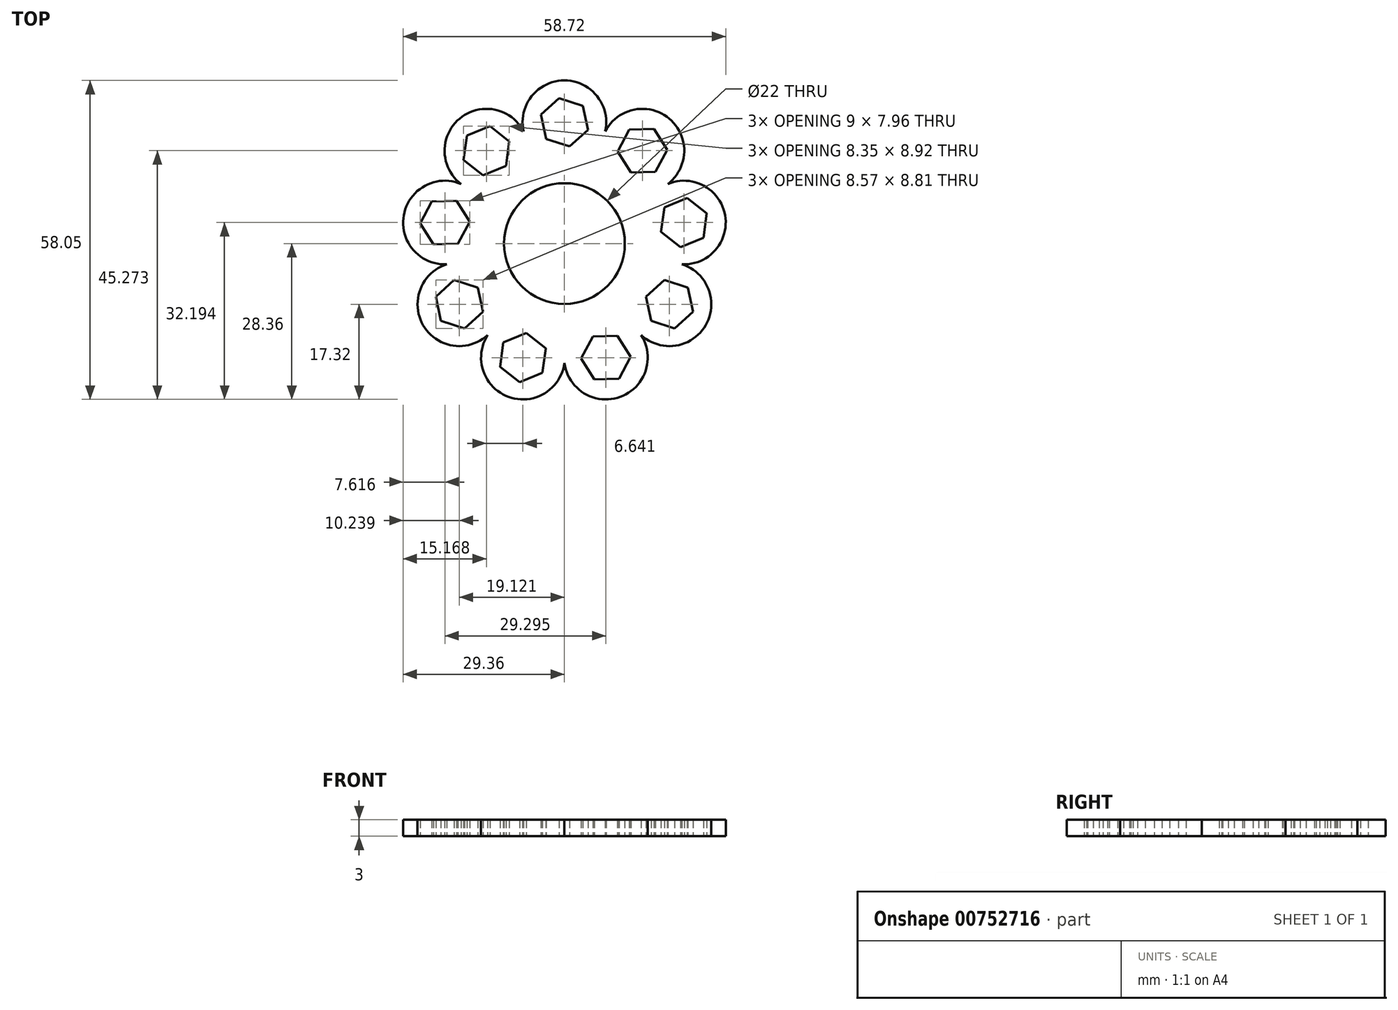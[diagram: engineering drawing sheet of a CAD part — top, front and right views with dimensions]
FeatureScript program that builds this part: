
annotation { "Feature Type Name" : "Feature", "Feature Type Description" : "" }
export const myFeature = defineFeature(function(context is Context, id is Id, definition is map)
    precondition{}
    {
        {
            var Q0;
            Q0=qCreatedBy(makeId("Top.planeOp"),FACE);
            var sketch = newSketch(context, id + "F0", { "sketchPlane" : qUnion([Q0])});
            skLineSegment(sketch, "E0.0", {"start": v(4.28, 20.7) * mm, "end": v(0.94, 17.68) * mm});
            skLineSegment(sketch, "E0.1", {"start": v(0.94, 17.68) * mm, "end": v(-3.34, 19.06) * mm});
            skLineSegment(sketch, "E0.2", {"start": v(-3.34, 19.06) * mm, "end": v(-4.28, 23.47) * mm});
            skLineSegment(sketch, "E0.3", {"start": v(-4.28, 23.47) * mm, "end": v(-0.94, 26.48) * mm});
            skLineSegment(sketch, "E0.4", {"start": v(-0.94, 26.48) * mm, "end": v(3.34, 25.1) * mm});
            skLineSegment(sketch, "E0.5", {"start": v(3.34, 25.1) * mm, "end": v(4.28, 20.7) * mm});
            skPoint(sketch, "E1.1.0", {"position": v(-10.33, 16.38) * mm});
            skLineSegment(sketch, "E1.1.1", {"start": v(-13.57, 21.37) * mm, "end": v(-10.02, 18.6) * mm});
            skLineSegment(sketch, "E1.1.5", {"start": v(-14.81, 12.45) * mm, "end": v(-18.37, 15.22) * mm});
            skLineSegment(sketch, "E1.1.6", {"start": v(-10.64, 14.15) * mm, "end": v(-14.81, 12.45) * mm});
            skLineSegment(sketch, "E1.1.7", {"start": v(-18.37, 15.22) * mm, "end": v(-17.74, 19.68) * mm});
            skLineSegment(sketch, "E1.1.9", {"start": v(-10.02, 18.6) * mm, "end": v(-10.64, 14.15) * mm});
            skLineSegment(sketch, "E1.1.10", {"start": v(-17.74, 19.68) * mm, "end": v(-13.57, 21.37) * mm});
            skPoint(sketch, "E1.2.0", {"position": v(-18.44, 5.9) * mm});
            skLineSegment(sketch, "E1.2.1", {"start": v(-24.13, 7.65) * mm, "end": v(-19.63, 7.81) * mm});
            skLineSegment(sketch, "E1.2.5", {"start": v(-19.35, 0.02) * mm, "end": v(-23.85, -0.14) * mm});
            skLineSegment(sketch, "E1.2.6", {"start": v(-17.24, 4) * mm, "end": v(-19.35, 0.02) * mm});
            skLineSegment(sketch, "E1.2.7", {"start": v(-23.85, -0.14) * mm, "end": v(-26.24, 3.67) * mm});
            skLineSegment(sketch, "E1.2.9", {"start": v(-19.63, 7.81) * mm, "end": v(-17.24, 4) * mm});
            skLineSegment(sketch, "E1.2.10", {"start": v(-26.24, 3.67) * mm, "end": v(-24.13, 7.65) * mm});
            skPoint(sketch, "E1.3.0", {"position": v(-17.92, -7.33) * mm});
            skLineSegment(sketch, "E1.3.1", {"start": v(-23.4, -9.65) * mm, "end": v(-20.06, -6.64) * mm});
            skLineSegment(sketch, "E1.3.5", {"start": v(-14.84, -12.43) * mm, "end": v(-18.18, -15.44) * mm});
            skLineSegment(sketch, "E1.3.6", {"start": v(-15.78, -8.02) * mm, "end": v(-14.84, -12.43) * mm});
            skLineSegment(sketch, "E1.3.7", {"start": v(-18.18, -15.44) * mm, "end": v(-22.46, -14.06) * mm});
            skLineSegment(sketch, "E1.3.9", {"start": v(-20.06, -6.64) * mm, "end": v(-15.78, -8.02) * mm});
            skLineSegment(sketch, "E1.3.10", {"start": v(-22.46, -14.06) * mm, "end": v(-23.4, -9.65) * mm});
            skPoint(sketch, "E1.4.0", {"position": v(-9.02, -17.13) * mm});
            skLineSegment(sketch, "E1.4.1", {"start": v(-11.72, -22.44) * mm, "end": v(-11.1, -17.98) * mm});
            skLineSegment(sketch, "E1.4.5", {"start": v(-3.38, -19.06) * mm, "end": v(-4, -23.52) * mm});
            skLineSegment(sketch, "E1.4.6", {"start": v(-6.93, -16.29) * mm, "end": v(-3.38, -19.06) * mm});
            skLineSegment(sketch, "E1.4.7", {"start": v(-4, -23.52) * mm, "end": v(-8.17, -25.2) * mm});
            skLineSegment(sketch, "E1.4.9", {"start": v(-11.1, -17.98) * mm, "end": v(-6.93, -16.29) * mm});
            skLineSegment(sketch, "E1.4.10", {"start": v(-8.17, -25.2) * mm, "end": v(-11.72, -22.44) * mm});
            skPoint(sketch, "E1.5.0", {"position": v(4.1, -18.92) * mm});
            skLineSegment(sketch, "E1.5.1", {"start": v(5.44, -24.73) * mm, "end": v(3.05, -20.9) * mm});
            skLineSegment(sketch, "E1.5.5", {"start": v(9.66, -16.77) * mm, "end": v(12.05, -20.58) * mm});
            skLineSegment(sketch, "E1.5.6", {"start": v(5.16, -16.93) * mm, "end": v(9.66, -16.77) * mm});
            skLineSegment(sketch, "E1.5.7", {"start": v(12.05, -20.58) * mm, "end": v(9.94, -24.56) * mm});
            skLineSegment(sketch, "E1.5.9", {"start": v(3.05, -20.9) * mm, "end": v(5.16, -16.93) * mm});
            skLineSegment(sketch, "E1.5.10", {"start": v(9.94, -24.56) * mm, "end": v(5.44, -24.73) * mm});
            skPoint(sketch, "E1.6.0", {"position": v(15.3, -11.85) * mm});
            skLineSegment(sketch, "E1.6.1", {"start": v(20.06, -15.44) * mm, "end": v(15.78, -14.06) * mm});
            skLineSegment(sketch, "E1.6.5", {"start": v(18.18, -6.64) * mm, "end": v(22.46, -8.02) * mm});
            skLineSegment(sketch, "E1.6.6", {"start": v(14.84, -9.65) * mm, "end": v(18.18, -6.64) * mm});
            skLineSegment(sketch, "E1.6.7", {"start": v(22.46, -8.02) * mm, "end": v(23.4, -12.43) * mm});
            skLineSegment(sketch, "E1.6.9", {"start": v(15.78, -14.06) * mm, "end": v(14.84, -9.65) * mm});
            skLineSegment(sketch, "E1.6.10", {"start": v(23.4, -12.43) * mm, "end": v(20.06, -15.44) * mm});
            skLineSegment(sketch, "E1.7.1", {"start": v(25.3, 1.07) * mm, "end": v(21.12, -0.63) * mm});
            skLineSegment(sketch, "E1.7.5", {"start": v(18.2, 6.6) * mm, "end": v(22.36, 8.3) * mm});
            skLineSegment(sketch, "E1.7.6", {"start": v(17.57, 2.14) * mm, "end": v(18.2, 6.6) * mm});
            skLineSegment(sketch, "E1.7.7", {"start": v(22.36, 8.3) * mm, "end": v(25.92, 5.53) * mm});
            skLineSegment(sketch, "E1.7.9", {"start": v(21.12, -0.63) * mm, "end": v(17.57, 2.14) * mm});
            skLineSegment(sketch, "E1.7.10", {"start": v(25.92, 5.53) * mm, "end": v(25.3, 1.07) * mm});
            skPoint(sketch, "E1.8.0", {"position": v(14.33, 13.02) * mm});
            skLineSegment(sketch, "E1.8.1", {"start": v(18.7, 17.08) * mm, "end": v(16.58, 13.1) * mm});
            skLineSegment(sketch, "E1.8.5", {"start": v(9.7, 16.75) * mm, "end": v(11.8, 20.73) * mm});
            skLineSegment(sketch, "E1.8.6", {"start": v(12.08, 12.93) * mm, "end": v(9.7, 16.75) * mm});
            skLineSegment(sketch, "E1.8.7", {"start": v(11.8, 20.73) * mm, "end": v(16.3, 20.9) * mm});
            skLineSegment(sketch, "E1.8.9", {"start": v(16.58, 13.1) * mm, "end": v(12.08, 12.93) * mm});
            skLineSegment(sketch, "E1.8.10", {"start": v(16.3, 20.9) * mm, "end": v(18.7, 17.08) * mm});
            skArc(sketch, "E2.trimOffspring", {"start": v(7.43, 20.41) * mm, "mid": v(0, 29.7) * mm, "end": v(-7.43, 20.41) * mm});
            skArc(sketch, "E3.trimOffspring", {"start": v(18.81, 10.86) * mm, "mid": v(19.09, 22.75) * mm, "end": v(7.43, 20.41) * mm});
            skArc(sketch, "E4.trimOffspring", {"start": v(21.4, -3.77) * mm, "mid": v(29.24, 5.16) * mm, "end": v(18.81, 10.86) * mm});
            skArc(sketch, "E5.trimOffspring", {"start": v(13.96, -16.64) * mm, "mid": v(25.72, -14.85) * mm, "end": v(21.4, -3.77) * mm});
            skArc(sketch, "E6.trimOffspring", {"start": v(0, -21.72) * mm, "mid": v(10.16, -27.9) * mm, "end": v(13.96, -16.64) * mm});
            skArc(sketch, "E7.trimOffspring", {"start": v(-13.96, -16.64) * mm, "mid": v(-10.16, -27.9) * mm, "end": v(0, -21.72) * mm});
            skArc(sketch, "E8.trimOffspring", {"start": v(-21.4, -3.77) * mm, "mid": v(-25.72, -14.85) * mm, "end": v(-13.96, -16.64) * mm});
            skArc(sketch, "E9.trimOffspring", {"start": v(-18.81, 10.86) * mm, "mid": v(-29.24, 5.16) * mm, "end": v(-21.4, -3.77) * mm});
            skArc(sketch, "E10.trimOffspring", {"start": v(-7.43, 20.41) * mm, "mid": v(-19.09, 22.75) * mm, "end": v(-18.81, 10.86) * mm});
            skCircle(sketch, "E11", {"center": v(0, 0) * mm, "radius": 11 * mm});
            skSolve(sketch);
        }
        {
            var Q0;
            Q0 = qSketchRegion(id + "F0", true);
            extrude(context, id + "F1", {"entities" : qUnion([Q0]), "depth" : 3 * mm, "offsetDistance" : 25 * mm});
        }
    });
